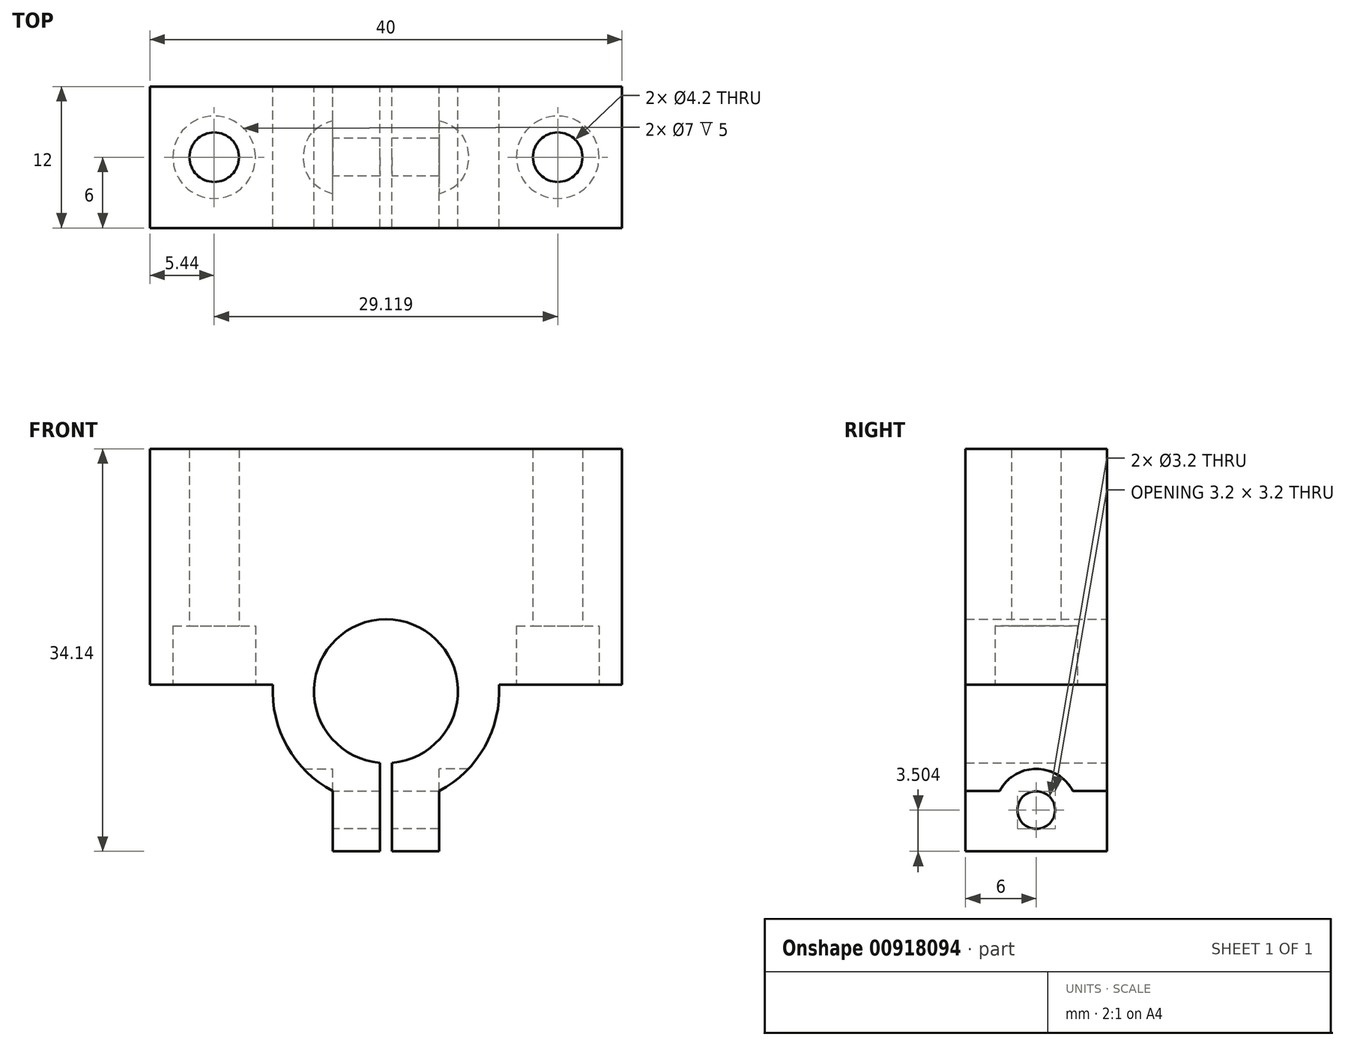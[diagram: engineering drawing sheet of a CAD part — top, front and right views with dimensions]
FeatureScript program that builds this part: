
annotation { "Feature Type Name" : "Feature", "Feature Type Description" : "" }
export const myFeature = defineFeature(function(context is Context, id is Id, definition is map)
    precondition{}
    {
        {
            var Q0;
            Q0=qCreatedBy(makeId("Front.planeOp"),FACE);
            var sketch = newSketch(context, id + "F0", { "sketchPlane" : qUnion([Q0])});
            skArc(sketch, "E0", {"start": v(0.5, -6.08) * mm, "mid": v(0, 6.1) * mm, "end": v(-0.5, -6.08) * mm});
            skLineSegment(sketch, "E1", {"start": v(-6.1, 0) * mm, "end": v(-9.6, 0) * mm});
            skLineSegment(sketch, "E2", {"start": v(6.1, 0) * mm, "end": v(9.6, 0) * mm});
            skArc(sketch, "E3", {"start": v(4.5, -8.48) * mm, "mid": v(0, 9.6) * mm, "end": v(-4.5, -8.48) * mm});
            skLineSegment(sketch, "E4", {"start": v(0, 0) * mm, "end": v(0, 3) * mm});
            skLineSegment(sketch, "E5", {"start": v(-5.31, 3) * mm, "end": v(-20, 3) * mm});
            skLineSegment(sketch, "E6", {"start": v(5.31, 3) * mm, "end": v(20, 3) * mm});
            skLineSegment(sketch, "E7", {"start": v(-20, 3) * mm, "end": v(-20, 13) * mm});
            skLineSegment(sketch, "E8", {"start": v(-20, 13) * mm, "end": v(20, 13) * mm});
            skLineSegment(sketch, "E9", {"start": v(20, 13) * mm, "end": v(20, 3) * mm});
            skLineSegment(sketch, "E10", {"start": v(0, 0) * mm, "end": v(-0.5, 0) * mm});
            skLineSegment(sketch, "E11", {"start": v(0, 0) * mm, "end": v(0.5, 0) * mm});
            skLineSegment(sketch, "E12", {"start": v(4.5, -13.59) * mm, "end": v(4.5, -8.48) * mm});
            skLineSegment(sketch, "E13", {"start": v(-4.5, -13.59) * mm, "end": v(-4.5, -8.48) * mm});
            skLineSegment(sketch, "E14", {"start": v(-0.5, -6.08) * mm, "end": v(-0.5, -13.59) * mm});
            skLineSegment(sketch, "E15", {"start": v(0.5, -6.08) * mm, "end": v(0.5, -13.59) * mm});
            skLineSegment(sketch, "E16", {"start": v(0.5, -13.59) * mm, "end": v(4.5, -13.59) * mm});
            skLineSegment(sketch, "E17", {"start": v(-0.5, -13.59) * mm, "end": v(-4.5, -13.59) * mm});
            skSolve(sketch);
        }
        {
            var Q0;
            Q0=qSketchRegion(id+"F0",true);
            extrude(context, id + "F1", {"entities" : qUnion([Q0]), "depth" : 12 * mm});
        }
        {
            var Q0;
            Q0=makeQuery(id+"F1.opExtrude","SWEPT_FACE",FACE,{"disambiguationData":[OSD([sQuery(id+"F0.wireOp",EDGE,"E5")])]});
            var sketch = newSketch(context, id + "F2", { "sketchPlane" : qUnion([Q0])});
            skLineSegment(sketch, "E18", {"start": v(-14.56, 12) * mm, "end": v(-14.56, 0) * mm});
            skCircle(sketch, "E19", {"center": v(-14.56, 6) * mm, "radius": 2.1 * mm});
            skSolve(sketch);
        }
        {
            var Q0;
            Q0=qSketchRegion(id+"F2",true);
            extrude(context, id + "F3", {"entities" : qUnion([Q0]), "operationType" : NewBodyOperationType.REMOVE, "oppositeDirection" : true, "depth" : 25 * mm});
        }
        {
            var Q0;
            Q0=makeQuery(id+"F1.opExtrude","SWEPT_FACE",FACE,{"disambiguationData":[OSD([sQuery(id+"F0.wireOp",EDGE,"E6")])]});
            var sketch = newSketch(context, id + "F4", { "sketchPlane" : qUnion([Q0])});
            skLineSegment(sketch, "E20", {"start": v(14.56, 12) * mm, "end": v(14.56, 0) * mm});
            skCircle(sketch, "E21", {"center": v(14.56, 6) * mm, "radius": 2.1 * mm});
            skSolve(sketch);
        }
        {
            var Q0;
            Q0=qSketchRegion(id+"F4",true);
            extrude(context, id + "F5", {"entities" : qUnion([Q0]), "operationType" : NewBodyOperationType.REMOVE, "oppositeDirection" : true, "depth" : 25 * mm});
        }
        {
            var Q0;
            Q0=makeQuery(id+"F1.opExtrude","SWEPT_FACE",FACE,{"disambiguationData":[OSD([sQuery(id+"F0.wireOp",EDGE,"E13")])]});
            var sketch = newSketch(context, id + "F6", { "sketchPlane" : qUnion([Q0])});
            skLineSegment(sketch, "E22", {"start": v(6, -13.59) * mm, "end": v(6, -6.59) * mm});
            skCircle(sketch, "E23", {"center": v(6, -10.09) * mm, "radius": 1.6 * mm});
            skSolve(sketch);
        }
        {
            var Q0;
            Q0=qSketchRegion(id+"F6",true);
            extrude(context, id + "F7", {"entities" : qUnion([Q0]), "operationType" : NewBodyOperationType.REMOVE, "oppositeDirection" : true, "depth" : 25 * mm});
        }
        {
            var Q0;
            Q0=makeQuery(id+"F1.opExtrude","SWEPT_FACE",FACE,{"disambiguationData":[OSD([sQuery(id+"F0.wireOp",EDGE,"E13")])]});
            var sketch = newSketch(context, id + "F8", { "sketchPlane" : qUnion([Q0])});
            skCircle(sketch, "E24", {"center": v(6, -10.09) * mm, "radius": 3.5 * mm});
            skSolve(sketch);
        }
        {
            var Q0;
            Q0=qSketchRegion(id+"F8",true);
            extrude(context, id + "F9", {"entities" : qUnion([Q0]), "operationType" : NewBodyOperationType.REMOVE, "depth" : 25 * mm});
        }
        {
            var Q0;
            Q0=makeQuery(id+"F1.opExtrude","SWEPT_FACE",FACE,{"disambiguationData":[OSD([sQuery(id+"F0.wireOp",EDGE,"E12")])]});
            var sketch = newSketch(context, id + "F10", { "sketchPlane" : qUnion([Q0])});
            skCircle(sketch, "E25", {"center": v(-6, -10.09) * mm, "radius": 3.5 * mm});
            skSolve(sketch);
        }
        {
            var Q0;
            Q0=qSketchRegion(id+"F10",true);
            extrude(context, id + "F11", {"entities" : qUnion([Q0]), "operationType" : NewBodyOperationType.REMOVE, "depth" : 25 * mm});
        }
        {
            var Q0;
            Q0=qSketchRegion(id+"F8",true);
            extrude(context, id + "F12", {"entities" : qUnion([Q0]), "operationType" : NewBodyOperationType.REMOVE, "depth" : 25 * mm});
        }
        {
            var Q0;
            Q0=makeQuery(id+"F1.opExtrude","SWEPT_FACE",FACE,{"disambiguationData":[OSD([sQuery(id+"F0.wireOp",EDGE,"E8")])]});
            var sketch = newSketch(context, id + "F13", { "sketchPlane" : qUnion([Q0])});
            skLineSegment(sketch, "E26.bottom", {"start": v(20, -12) * mm, "end": v(-20, -12) * mm});
            skLineSegment(sketch, "E26.top", {"start": v(20, 0) * mm, "end": v(-20, 0) * mm});
            skLineSegment(sketch, "E26.left", {"start": v(20, -12) * mm, "end": v(20, 0) * mm});
            skLineSegment(sketch, "E26.right", {"start": v(-20, -12) * mm, "end": v(-20, 0) * mm});
            skCircle(sketch, "E27", {"center": v(14.56, -6) * mm, "radius": 2.1 * mm});
            skCircle(sketch, "E28", {"center": v(-14.56, -6) * mm, "radius": 2.1 * mm});
            skSolve(sketch);
        }
        {
            var Q0;
            Q0=qSketchRegion(id+"F13",true);
            extrude(context, id + "F14", {"entities" : qUnion([Q0]), "operationType" : NewBodyOperationType.ADD, "depth" : 7.55 * mm});
        }
        {
            var Q0;
            Q0=makeQuery(id+"F1.opExtrude","SWEPT_FACE",FACE,{"disambiguationData":[OSD([sQuery(id+"F0.wireOp",EDGE,"E5")])]});
            var sketch = newSketch(context, id + "F15", { "sketchPlane" : qUnion([Q0])});
            skLineSegment(sketch, "E29.bottom", {"start": v(-20, 12) * mm, "end": v(-9.12, 12) * mm});
            skLineSegment(sketch, "E29.top", {"start": v(-20, 0) * mm, "end": v(-9.12, 0) * mm});
            skLineSegment(sketch, "E29.left", {"start": v(-20, 12) * mm, "end": v(-20, 0) * mm});
            skLineSegment(sketch, "E29.right", {"start": v(-9.12, 12) * mm, "end": v(-9.12, 0) * mm});
            skCircle(sketch, "E30", {"center": v(-14.56, 6) * mm, "radius": 2.1 * mm});
            skSolve(sketch);
        }
        {
            var Q0;
            Q0=makeQuery(id+"F1.opExtrude","SWEPT_FACE",FACE,{"disambiguationData":[OSD([sQuery(id+"F0.wireOp",EDGE,"E6")])]});
            var sketch = newSketch(context, id + "F16", { "sketchPlane" : qUnion([Q0])});
            skLineSegment(sketch, "E31.bottom", {"start": v(20, 12) * mm, "end": v(9.12, 12) * mm});
            skLineSegment(sketch, "E31.top", {"start": v(20, 0) * mm, "end": v(9.12, 0) * mm});
            skLineSegment(sketch, "E31.left", {"start": v(20, 12) * mm, "end": v(20, 0) * mm});
            skLineSegment(sketch, "E31.right", {"start": v(9.12, 12) * mm, "end": v(9.12, 0) * mm});
            skCircle(sketch, "E32", {"center": v(14.56, 6) * mm, "radius": 2.1 * mm});
            skSolve(sketch);
        }
        {
            var Q0;
            Q0=qSketchRegion(id+"F16",true);
            var Q1;
            Q1=makeQuery(id+"F15.imprint","IMPRINT",FACE,{"disambiguationData":[TD([[makeQuery(id+"F15.imprint","IMPRINT",EDGE,{"derivedFrom":sQuery(id+"F15.wireOp",EDGE,"E29.bottom")}),1.0]])]});
            extrude(context, id + "F17", {"entities" : qUnion([Q0, Q1]), "operationType" : NewBodyOperationType.ADD, "depth" : 2.45 * mm});
        }
        {
            var Q0;
            Q0=makeQuery(id+"F17.opExtrude","CAP_FACE",FACE,{"disambiguationData":[OSD([sQuery(id+"F15.wireOp",EDGE,"E29.bottom"),sQuery(id+"F15.wireOp",EDGE,"E29.top"),sQuery(id+"F15.wireOp",EDGE,"E29.left"),sQuery(id+"F15.wireOp",EDGE,"E29.right"),sQuery(id+"F15.wireOp",EDGE,"E30")])],"isStart":false});
            var sketch = newSketch(context, id + "F18", { "sketchPlane" : qUnion([Q0])});
            skCircle(sketch, "E33", {"center": v(-14.56, 6) * mm, "radius": 3.5 * mm});
            skSolve(sketch);
        }
        {
            var Q0;
            Q0=makeQuery(id+"F17.opExtrude","CAP_FACE",FACE,{"disambiguationData":[OSD([sQuery(id+"F16.wireOp",EDGE,"E31.bottom"),sQuery(id+"F16.wireOp",EDGE,"E31.top"),sQuery(id+"F16.wireOp",EDGE,"E31.left"),sQuery(id+"F16.wireOp",EDGE,"E31.right"),sQuery(id+"F16.wireOp",EDGE,"E32")])],"isStart":false});
            var sketch = newSketch(context, id + "F19", { "sketchPlane" : qUnion([Q0])});
            skCircle(sketch, "E34", {"center": v(14.56, 6) * mm, "radius": 3.5 * mm});
            skSolve(sketch);
        }
        {
            var Q0;
            Q0=qSketchRegion(id+"F19",true);
            var Q1;
            Q1=qSketchRegion(id+"F18",true);
            extrude(context, id + "F20", {"entities" : qUnion([Q0, Q1]), "operationType" : NewBodyOperationType.REMOVE, "oppositeDirection" : true, "depth" : 5 * mm});
        }
    });
